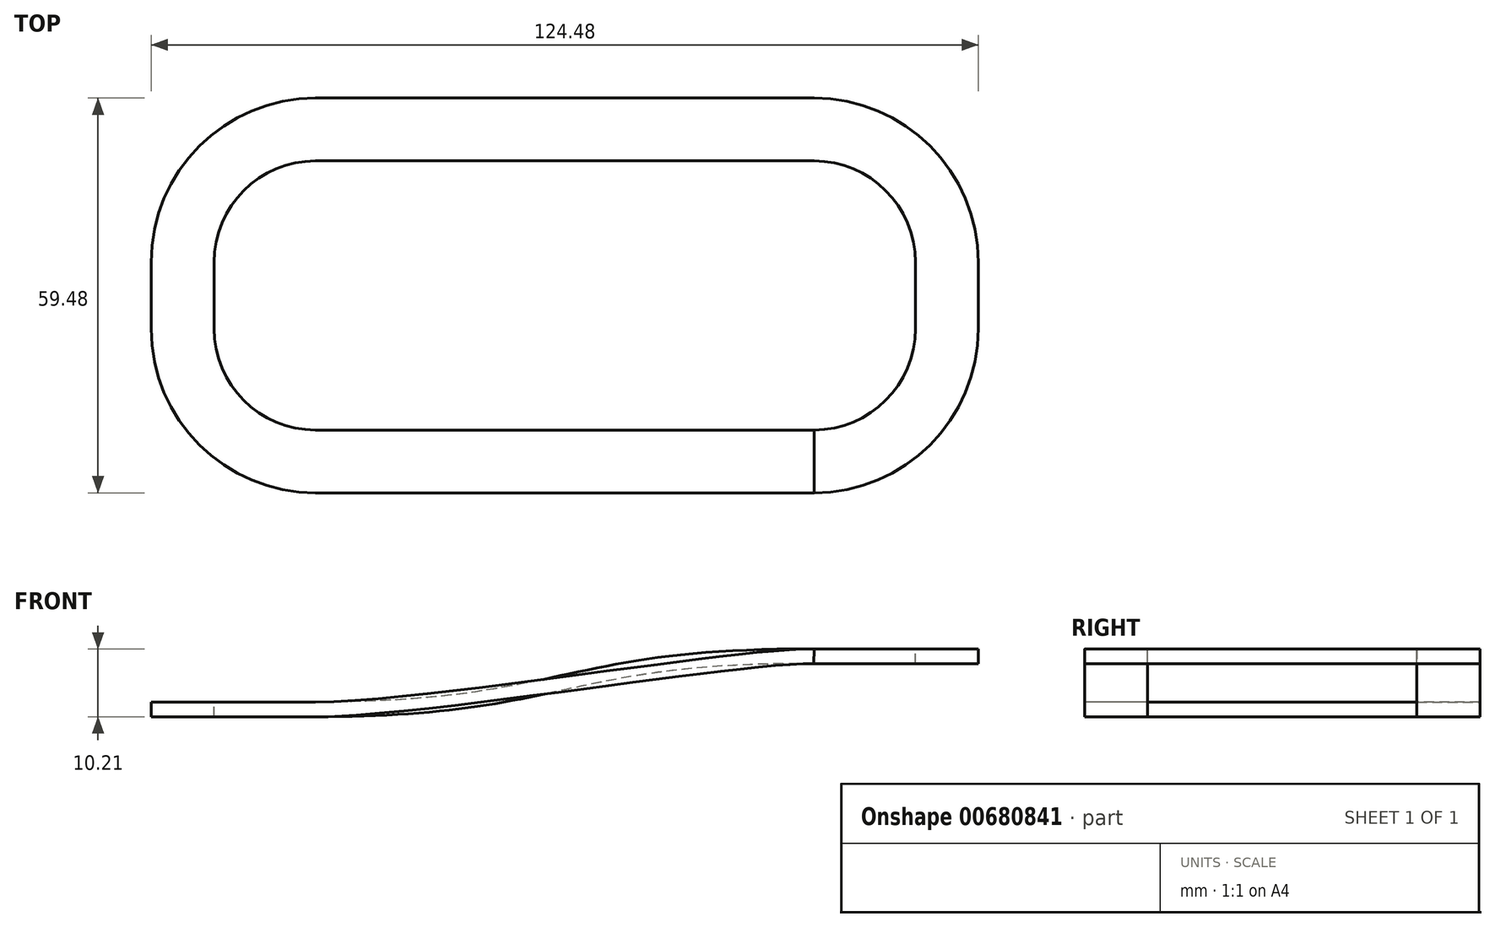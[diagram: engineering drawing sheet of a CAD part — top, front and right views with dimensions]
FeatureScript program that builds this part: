
annotation { "Feature Type Name" : "Feature", "Feature Type Description" : "" }
export const myFeature = defineFeature(function(context is Context, id is Id, definition is map)
    precondition{}
    {
        {
            var Q0;
            Q0=qCreatedBy(makeId("Top.planeOp"),FACE);
            var sketch = newSketch(context, id + "F0", { "sketchPlane" : qUnion([Q0])});
            skLineSegment(sketch, "E0.bottom", {"start": v(62.5, -30) * mm, "end": v(-62.5, -30) * mm, "construction": true});
            skLineSegment(sketch, "E0.top", {"start": v(62.5, 30) * mm, "end": v(-62.5, 30) * mm, "construction": true});
            skLineSegment(sketch, "E0.left", {"start": v(62.5, -30) * mm, "end": v(62.5, 30) * mm, "construction": true});
            skLineSegment(sketch, "E0.right", {"start": v(-62.5, -30) * mm, "end": v(-62.5, 30) * mm, "construction": true});
            skLineSegment(sketch, "E1.bottom", {"start": v(37.5, -25) * mm, "end": v(-37.5, -25) * mm, "construction": true});
            skLineSegment(sketch, "E1.top", {"start": v(37.5, 25) * mm, "end": v(-37.5, 25) * mm, "construction": true});
            skLineSegment(sketch, "E1.left", {"start": v(57.5, -5) * mm, "end": v(57.5, 5) * mm, "construction": true});
            skLineSegment(sketch, "E1.right", {"start": v(-57.5, -5) * mm, "end": v(-57.5, 5) * mm});
            skPoint(sketch, "E1.middle", {"position": v(0, 0) * mm});
            skPoint(sketch, "E2.visualSharp", {"position": v(-57.5, 25) * mm});
            skLineSegment(sketch, "E2.filletArc", {"start": v(-37.5, 25) * mm, "end": v(-37.5, 25) * mm});
            skPoint(sketch, "E3.visualSharp", {"position": v(-57.5, -25) * mm});
            skArc(sketch, "E3.filletArc", {"start": v(-57.5, -5) * mm, "mid": v(-51.64, -19.14) * mm, "end": v(-37.5, -25) * mm});
            skPoint(sketch, "E4.visualSharp", {"position": v(57.5, -25) * mm});
            skArc(sketch, "E4.filletArc", {"start": v(37.5, -25) * mm, "mid": v(51.64, -19.14) * mm, "end": v(57.5, -5) * mm, "construction": true});
            skPoint(sketch, "E5.visualSharp", {"position": v(57.5, 25) * mm});
            skArc(sketch, "E5.filletArc", {"start": v(57.5, 5) * mm, "mid": v(51.64, 19.14) * mm, "end": v(37.5, 25) * mm, "construction": true});
            skPoint(sketch, "E6", {"position": v(57.5, 0) * mm});
            skPoint(sketch, "E7", {"position": v(-51.64, 19.14) * mm});
            skPoint(sketch, "E8", {"position": v(-51.64, -19.14) * mm});
            skLineSegment(sketch, "E9", {"start": v(-37.5, -25) * mm, "end": v(-37.5, -25) * mm});
            skArc(sketch, "E10", {"start": v(-37.5, 25) * mm, "mid": v(-51.64, 19.14) * mm, "end": v(-57.5, 5) * mm});
            skSolve(sketch);
        }
        {
            var Q0;
            Q0=sQuery(id+"F0.wireOp",EDGE,"E1.left");
            var Q1;
            Q1=sQuery(id+"F0.wireOp",VERTEX,"E6");
            cPlane(context, id + "F1", {"entities" : qUnion([Q0, Q1]), "cplaneType" : CPlaneType.CURVE_POINT, "offset" : 25 * mm, "width" : 150 * mm, "height" : 150 * mm});
        }
        {
            var Q0;
            Q0=qCreatedBy(id+"F1.planeOp",FACE);
            var sketch = newSketch(context, id + "F2", { "sketchPlane" : qUnion([Q0])});
            skPoint(sketch, "E11", {"position": v(-57.5, 8) * mm});
            skSolve(sketch);
        }
        {
            var Q0;
            Q0=sQuery(id+"F0.wireOp",EDGE,"E1.bottom");
            var Q1;
            Q1=sQuery(id+"F0.wireOp",VERTEX,"E1.bottom.start");
            cPlane(context, id + "F3", {"entities" : qUnion([Q0, Q1]), "cplaneType" : CPlaneType.CURVE_POINT, "offset" : 25 * mm, "width" : 150 * mm, "height" : 150 * mm});
        }
        {
            var Q0;
            Q0=qCreatedBy(id+"F3.planeOp",FACE);
            var sketch = newSketch(context, id + "F4", { "sketchPlane" : qUnion([Q0])});
            skPoint(sketch, "E12", {"position": v(25, 8) * mm});
            skPoint(sketch, "E13", {"position": v(-25, 8) * mm});
            skSolve(sketch);
        }
        {
            var Q0;
            Q0=sQuery(id+"F0.wireOp",VERTEX,"E1.bottom.end");
            var Q1;
            Q1=sQuery(id+"F0.wireOp",VERTEX,"E1.bottom.start");
            var Q2;
            Q2=sQuery(id+"F4.wireOp",VERTEX,"E12");
            cPlane(context, id + "F5", {"entities" : qUnion([Q0, Q1, Q2]), "cplaneType" : CPlaneType.THREE_POINT, "offset" : 25 * mm, "width" : 150 * mm, "height" : 150 * mm});
        }
        {
            var Q0;
            Q0=qCreatedBy(id+"F5.planeOp",FACE);
            var sketch = newSketch(context, id + "F6", { "sketchPlane" : qUnion([Q0])});
            skFitSpline(sketch, "E14", {"points": [v(37.5, 0) * mm, v(-37.5, 8) * mm], "startDerivative": vector(-48.99, 0) * mm, "endDerivative": vector(-34.15, -0.58) * mm});
            skSolve(sketch);
        }
        {
            var Q0;
            Q0=sQuery(id+"F4.wireOp",VERTEX,"E12");
            var Q1;
            Q1=sQuery(id+"F4.wireOp",VERTEX,"E13");
            var Q2;
            Q2=sQuery(id+"F2.wireOp",VERTEX,"E11");
            cPlane(context, id + "F7", {"entities" : qUnion([Q0, Q1, Q2]), "cplaneType" : CPlaneType.THREE_POINT, "offset" : 25 * mm, "width" : 150 * mm, "height" : 150 * mm});
        }
        {
            var Q0;
            Q0=qCreatedBy(id+"F7.planeOp",FACE);
            var sketch = newSketch(context, id + "F8", { "sketchPlane" : qUnion([Q0])});
            skArc(sketch, "E15", {"start": v(37.5, -25) * mm, "mid": v(51.64, -19.14) * mm, "end": v(57.5, -5) * mm});
            skLineSegment(sketch, "E16", {"start": v(57.5, -5) * mm, "end": v(57.5, 5) * mm});
            skArc(sketch, "E17", {"start": v(57.5, 5) * mm, "mid": v(51.64, 19.14) * mm, "end": v(37.5, 25) * mm});
            skSolve(sketch);
        }
        {
            var Q0;
            Q0=sQuery(id+"F4.wireOp",VERTEX,"E13");
            var Q1;
            Q1=sQuery(id+"F0.wireOp",VERTEX,"E5.filletArc.end");
            var Q2;
            Q2=sQuery(id+"F0.wireOp",VERTEX,"E1.top.end");
            cPlane(context, id + "F9", {"entities" : qUnion([Q0, Q1, Q2]), "cplaneType" : CPlaneType.THREE_POINT, "offset" : 25 * mm, "width" : 150 * mm, "height" : 150 * mm});
        }
        {
            var Q0;
            Q0=qCreatedBy(id+"F9.planeOp",FACE);
            var sketch = newSketch(context, id + "F10", { "sketchPlane" : qUnion([Q0])});
            skFitSpline(sketch, "E18", {"points": [v(37.5, 8) * mm, v(-37.5, 0) * mm], "startDerivative": vector(-112.5, 0.76) * mm, "endDerivative": vector(-112.5, 0) * mm});
            skSolve(sketch);
        }
        {
            var Q0;
            Q0=sQuery(id+"F2.wireOp",VERTEX,"E11");
            var Q1;
            Q1=sQuery(id+"F8.wireOp",EDGE,"E16");
            cPlane(context, id + "F11", {"entities" : qUnion([Q0, Q1]), "cplaneType" : CPlaneType.CURVE_POINT, "offset" : 25 * mm, "width" : 150 * mm, "height" : 150 * mm});
        }
        {
            var Q0;
            Q0=qCreatedBy(id+"F11.planeOp",FACE);
            var sketch = newSketch(context, id + "F12", { "sketchPlane" : qUnion([Q0])});
            skLineSegment(sketch, "E19.bottom", {"start": v(-52.76, 6.9) * mm, "end": v(-62.24, 6.9) * mm});
            skLineSegment(sketch, "E19.top", {"start": v(-52.76, 9.1) * mm, "end": v(-62.24, 9.1) * mm});
            skLineSegment(sketch, "E19.left", {"start": v(-52.76, 6.9) * mm, "end": v(-52.76, 9.1) * mm});
            skLineSegment(sketch, "E19.right", {"start": v(-62.24, 6.9) * mm, "end": v(-62.24, 9.1) * mm});
            skPoint(sketch, "E19.middle", {"position": v(-57.5, 8) * mm});
            skSolve(sketch);
        }
        {
            var Q0;
            Q0 = qSketchRegion(id + "F12", true);
            var Q1;
            Q1=sQuery(id+"F8.wireOp",EDGE,"E15");
            var Q2;
            Q2=sQuery(id+"F8.wireOp",EDGE,"E16");
            var Q3;
            Q3=sQuery(id+"F8.wireOp",EDGE,"E17");
            var Q4;
            Q4=sQuery(id+"F10.wireOp",EDGE,"E18");
            var Q5;
            Q5=sQuery(id+"F6.wireOp",EDGE,"E14");
            var Q6;
            Q6=sQuery(id+"F0.wireOp",EDGE,"E10");
            var Q7;
            Q7=sQuery(id+"F0.wireOp",EDGE,"E1.right");
            var Q8;
            Q8=sQuery(id+"F0.wireOp",EDGE,"E3.filletArc");
            sweep(context, id + "F13", {"profiles" : qUnion([Q0]), "path" : qUnion([Q1, Q2, Q3, Q4, Q5, Q6, Q7, Q8])});
        }
    });
